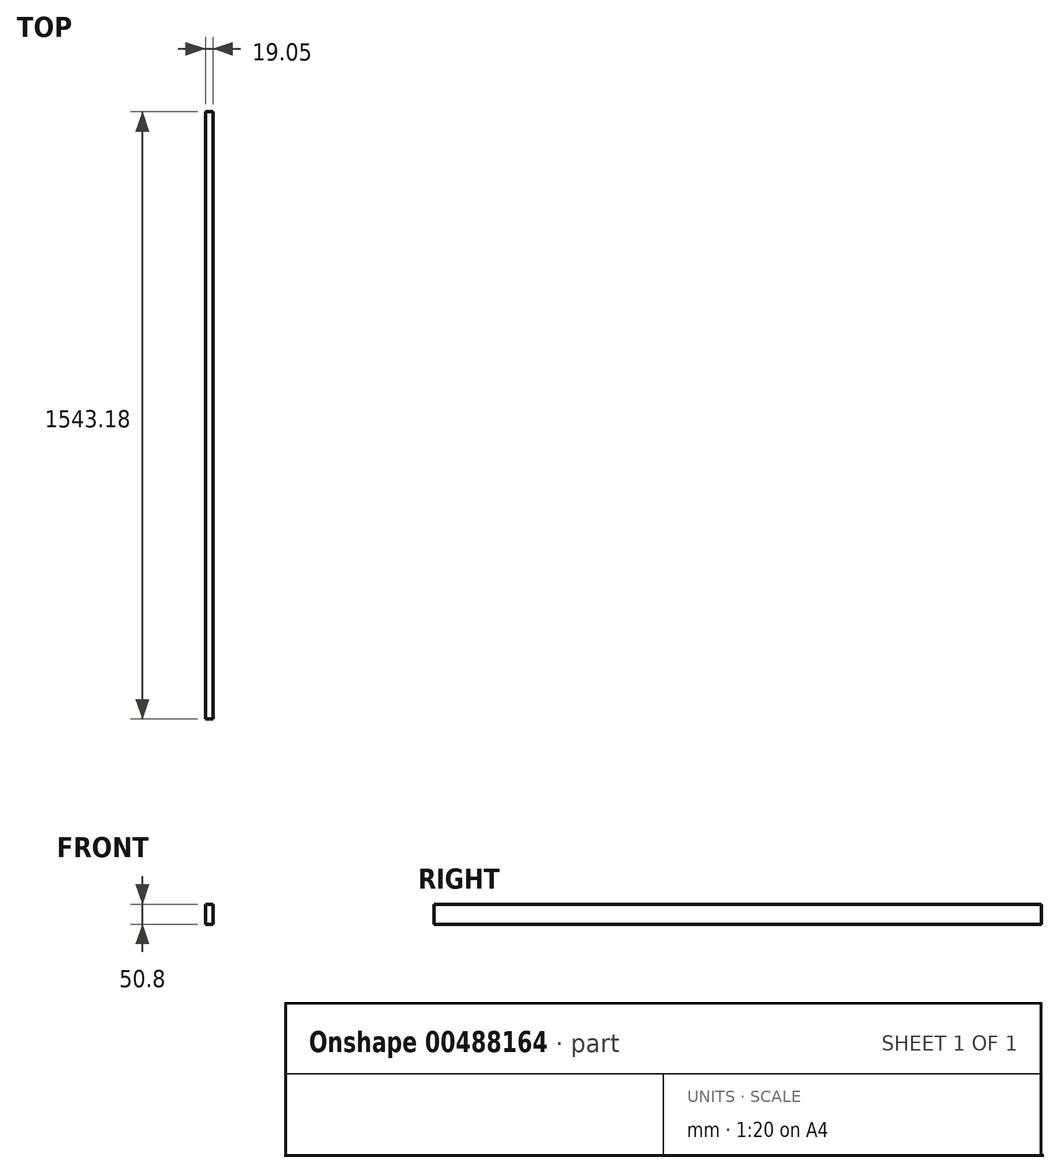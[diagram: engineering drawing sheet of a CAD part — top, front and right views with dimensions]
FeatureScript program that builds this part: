
annotation { "Feature Type Name" : "Feature", "Feature Type Description" : "" }
export const myFeature = defineFeature(function(context is Context, id is Id, definition is map)
    precondition{}
    {
        {
            var Q0;
            Q0=qCreatedBy(makeId("Front.planeOp"),FACE);
            var sketch = newSketch(context, id + "F0", { "sketchPlane" : qUnion([Q0])});
            skLineSegment(sketch, "E0", {"start": v(0, 0) * mm, "end": v(19.05, 0) * mm});
            skLineSegment(sketch, "E1", {"start": v(0, 0) * mm, "end": v(0, -50.8) * mm});
            skLineSegment(sketch, "E2", {"start": v(0, -50.8) * mm, "end": v(19.05, -50.8) * mm});
            skLineSegment(sketch, "E3", {"start": v(19.05, -50.8) * mm, "end": v(19.05, 0) * mm});
            skSolve(sketch);
        }
        {
            var Q0;
            Q0=makeQuery(id+"F0.imprint","IMPRINT",FACE,{"disambiguationData":[TD([[makeQuery(id+"F0.imprint","IMPRINT",EDGE,{"derivedFrom":sQuery(id+"F0.wireOp",EDGE,"E0")}),-1.0]])]});
            extrude(context, id + "F1", {"entities" : qUnion([Q0]), "oppositeDirection" : true, "depth" : 1543.18 * mm, "offsetDistance" : 25.4 * mm});
        }
    });
